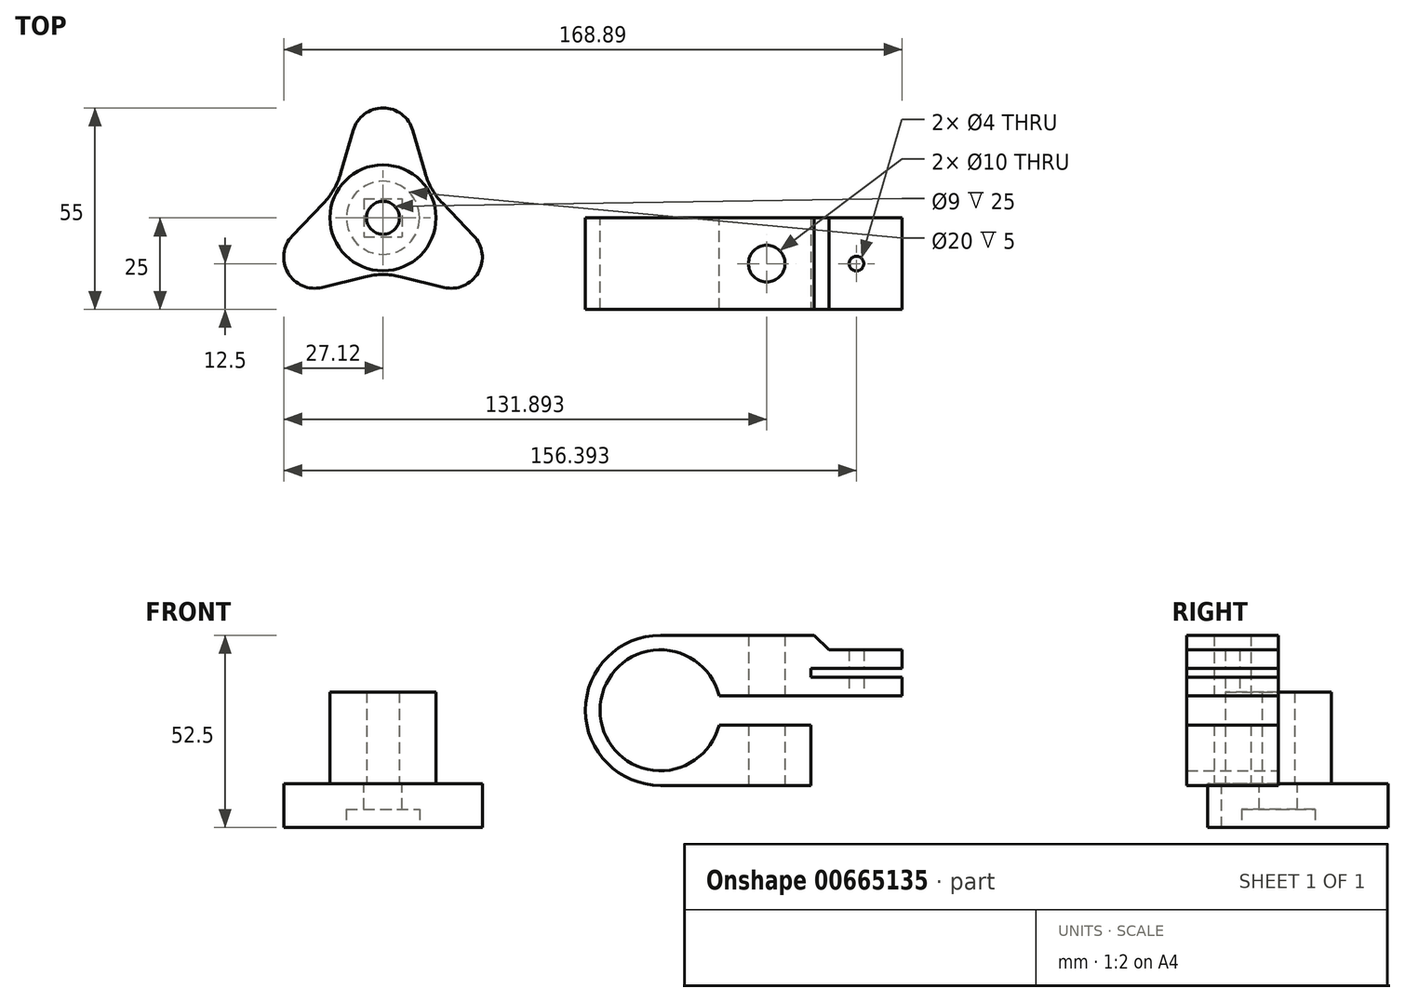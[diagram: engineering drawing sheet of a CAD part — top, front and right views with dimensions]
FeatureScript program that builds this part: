
annotation { "Feature Type Name" : "Feature", "Feature Type Description" : "" }
export const myFeature = defineFeature(function(context is Context, id is Id, definition is map)
    precondition{}
    {
        {
            var Q0;
            Q0=qCreatedBy(makeId("Top.planeOp"),FACE);
            var sketch = newSketch(context, id + "F0", { "sketchPlane" : qUnion([Q0])});
            skLineSegment(sketch, "E0.bottom", {"start": v(-5.25, 5.25) * mm, "end": v(5.25, 5.25) * mm});
            skLineSegment(sketch, "E0.top", {"start": v(-5.25, -5.25) * mm, "end": v(5.25, -5.25) * mm});
            skLineSegment(sketch, "E0.left", {"start": v(-5.25, 5.25) * mm, "end": v(-5.25, -5.25) * mm});
            skLineSegment(sketch, "E0.right", {"start": v(5.25, 5.25) * mm, "end": v(5.25, -5.25) * mm});
            skLineSegment(sketch, "E1", {"start": v(5.25, -5.25) * mm, "end": v(-5.25, 5.25) * mm, "construction": true});
            skCircle(sketch, "E2", {"center": v(0, 0) * mm, "radius": 14.47 * mm});
            skArc(sketch, "E3", {"start": v(8.15, 23.88) * mm, "mid": v(0, 30) * mm, "end": v(-8.15, 23.88) * mm});
            skLineSegment(sketch, "E4", {"start": v(-8.15, 23.88) * mm, "end": v(-11.53, 12.19) * mm});
            skLineSegment(sketch, "E5", {"start": v(8.15, 23.88) * mm, "end": v(11.53, 12.19) * mm});
            skArc(sketch, "E6.1.0", {"start": v(-24.75, -4.88) * mm, "mid": v(-25.98, -15) * mm, "end": v(-16.6, -19) * mm});
            skLineSegment(sketch, "E6.1.1", {"start": v(-24.75, -4.88) * mm, "end": v(-16.32, 3.9) * mm});
            skLineSegment(sketch, "E6.1.2", {"start": v(-16.6, -19) * mm, "end": v(-4.79, -16.08) * mm});
            skArc(sketch, "E6.2.0", {"start": v(16.6, -19) * mm, "mid": v(25.98, -15) * mm, "end": v(24.75, -4.88) * mm});
            skLineSegment(sketch, "E6.2.1", {"start": v(16.6, -19) * mm, "end": v(4.79, -16.08) * mm});
            skLineSegment(sketch, "E6.2.2", {"start": v(24.75, -4.88) * mm, "end": v(16.32, 3.9) * mm});
            skPoint(sketch, "E7.orphan", {"position": v(-10.43, 10.02) * mm});
            skPoint(sketch, "E8.orphan", {"position": v(-17.5, -8.42) * mm});
            skPoint(sketch, "E9.orphan", {"position": v(13.9, 4.02) * mm});
            skPoint(sketch, "E10.orphan", {"position": v(1.46, 19.36) * mm});
            skPoint(sketch, "E11.orphan", {"position": v(16.04, -10.94) * mm});
            skPoint(sketch, "E12.orphan", {"position": v(-3.46, -14.04) * mm});
            skPoint(sketch, "E13.visualSharp", {"position": v(-12.9, 7.45) * mm});
            skArc(sketch, "E13.filletArc", {"start": v(-16.32, 3.9) * mm, "mid": v(-13.42, 7.75) * mm, "end": v(-11.53, 12.19) * mm});
            skPoint(sketch, "E14.visualSharp", {"position": v(12.9, 7.45) * mm});
            skArc(sketch, "E14.filletArc", {"start": v(11.53, 12.19) * mm, "mid": v(13.42, 7.75) * mm, "end": v(16.32, 3.9) * mm});
            skPoint(sketch, "E15.visualSharp", {"position": v(0, -14.9) * mm});
            skArc(sketch, "E15.filletArc", {"start": v(4.79, -16.08) * mm, "mid": v(0, -15.5) * mm, "end": v(-4.79, -16.08) * mm});
            skCircle(sketch, "E16", {"center": v(0, 0) * mm, "radius": 4.5 * mm});
            skSolve(sketch);
        }
        {
            var Q0;
            Q0=makeQuery(id+"F0.imprint","IMPRINT",FACE,{"disambiguationData":[TD([[makeQuery(id+"F0.imprint","IMPRINT",EDGE,{"derivedFrom":sQuery(id+"F0.wireOp",EDGE,"E2")}),-1.0]])]});
            var Q1;
            Q1=makeQuery(id+"F0.imprint","IMPRINT",FACE,{"disambiguationData":[TD([[makeQuery(id+"F0.imprint","IMPRINT",EDGE,{"derivedFrom":sQuery(id+"F0.wireOp",EDGE,"E0.bottom")}),1.0]])]});
            extrude(context, id + "F1", {"entities" : qUnion([Q0, Q1]), "oppositeDirection" : true, "depth" : 12 * mm, "offsetDistance" : 25 * mm});
        }
        {
            var Q0;
            Q0=makeQuery(id+"F0.imprint","IMPRINT",FACE,{"disambiguationData":[TD([[makeQuery(id+"F0.imprint","IMPRINT",EDGE,{"derivedFrom":sQuery(id+"F0.wireOp",EDGE,"E0.bottom")}),1.0]])]});
            var Q1;
            Q1=makeQuery(id+"F0.imprint","IMPRINT",FACE,{"disambiguationData":[TD([[makeQuery(id+"F0.imprint","IMPRINT",EDGE,{"derivedFrom":sQuery(id+"F0.wireOp",EDGE,"E0.bottom")}),-1.0]])]});
            extrude(context, id + "F2", {"entities" : qUnion([Q0, Q1]), "operationType" : NewBodyOperationType.ADD, "depth" : 25 * mm, "offsetDistance" : 25 * mm});
        }
        {
            var Q0;
            Q0=makeQuery(id+"F1.opExtrude","CAP_FACE",FACE,{"disambiguationData":[OSD([sQuery(id+"F0.wireOp",EDGE,"E0.bottom"),sQuery(id+"F0.wireOp",EDGE,"E0.top"),sQuery(id+"F0.wireOp",EDGE,"E0.left"),sQuery(id+"F0.wireOp",EDGE,"E0.right"),sQuery(id+"F0.wireOp",EDGE,"E3"),sQuery(id+"F0.wireOp",EDGE,"E4"),sQuery(id+"F0.wireOp",EDGE,"E5"),sQuery(id+"F0.wireOp",EDGE,"E6.1.0"),sQuery(id+"F0.wireOp",EDGE,"E6.1.1"),sQuery(id+"F0.wireOp",EDGE,"E6.1.2"),sQuery(id+"F0.wireOp",EDGE,"E6.2.0"),sQuery(id+"F0.wireOp",EDGE,"E6.2.1"),sQuery(id+"F0.wireOp",EDGE,"E6.2.2"),sQuery(id+"F0.wireOp",EDGE,"E13.filletArc"),sQuery(id+"F0.wireOp",EDGE,"E14.filletArc"),sQuery(id+"F0.wireOp",EDGE,"E15.filletArc")])],"isStart":false});
            var sketch = newSketch(context, id + "F3", { "sketchPlane" : qUnion([Q0])});
            skCircle(sketch, "E17", {"center": v(0, 0) * mm, "radius": 10 * mm});
            skSolve(sketch);
        }
        {
            var Q0;
            Q0=makeQuery(id+"F3.imprint","IMPRINT",FACE,{"disambiguationData":[TD([[makeQuery(id+"F3.imprint","IMPRINT",EDGE,{"derivedFrom":sQuery(id+"F3.wireOp",EDGE,"E17")}),1.0]])]});
            extrude(context, id + "F4", {"entities" : qUnion([Q0]), "operationType" : NewBodyOperationType.REMOVE, "oppositeDirection" : true, "depth" : 5 * mm, "offsetDistance" : 25 * mm});
        }
        {
            var Q0;
            Q0=qCreatedBy(makeId("Front.planeOp"),FACE);
            var sketch = newSketch(context, id + "F5", { "sketchPlane" : qUnion([Q0])});
            skArc(sketch, "E18", {"start": v(91.77, 24) * mm, "mid": v(59.26, 20) * mm, "end": v(91.77, 16) * mm});
            skLineSegment(sketch, "E19", {"start": v(91.77, 24) * mm, "end": v(116.77, 24) * mm});
            skLineSegment(sketch, "E20", {"start": v(116.77, 24) * mm, "end": v(116.77, 40.5) * mm});
            skLineSegment(sketch, "E21", {"start": v(116.77, 40.5) * mm, "end": v(75.76, 40.5) * mm});
            skArc(sketch, "E22", {"start": v(75.76, 40.5) * mm, "mid": v(55.26, 20) * mm, "end": v(75.76, -0.5) * mm});
            skLineSegment(sketch, "E23", {"start": v(75.76, -0.5) * mm, "end": v(116.77, -0.5) * mm});
            skLineSegment(sketch, "E24", {"start": v(116.77, -0.5) * mm, "end": v(116.77, 16) * mm});
            skLineSegment(sketch, "E25", {"start": v(116.77, 16) * mm, "end": v(91.77, 16) * mm});
            skSolve(sketch);
        }
        {
            var Q0;
            Q0=makeQuery(id+"F5.imprint","IMPRINT",FACE,{"disambiguationData":[TD([[makeQuery(id+"F5.imprint","IMPRINT",EDGE,{"derivedFrom":sQuery(id+"F5.wireOp",EDGE,"E18")}),-1.0]])]});
            extrude(context, id + "F6", {"entities" : qUnion([Q0]), "depth" : 25 * mm, "offsetDistance" : 25 * mm});
        }
        {
            var Q0;
            Q0=makeQuery(id+"F6.opExtrude","SWEPT_FACE",FACE,{"disambiguationData":[OSD([sQuery(id+"F5.wireOp",EDGE,"E20")])]});
            var sketch = newSketch(context, id + "F7", { "sketchPlane" : qUnion([Q0])});
            skLineSegment(sketch, "E26.0", {"start": v(0, 24) * mm, "end": v(0, 40.5) * mm});
            skLineSegment(sketch, "E27.0", {"start": v(-25, 24) * mm, "end": v(0, 24) * mm});
            skLineSegment(sketch, "E28.0", {"start": v(-25, 24) * mm, "end": v(-25, 40.5) * mm});
            skLineSegment(sketch, "E29.0", {"start": v(-25, 40.5) * mm, "end": v(0, 40.5) * mm});
            skLineSegment(sketch, "E30", {"start": v(0, 29) * mm, "end": v(-25, 29) * mm});
            skLineSegment(sketch, "E31", {"start": v(0, 31.5) * mm, "end": v(-25, 31.5) * mm});
            skLineSegment(sketch, "E32", {"start": v(0, 36.5) * mm, "end": v(-25, 36.5) * mm});
            skLineSegment(sketch, "E33", {"start": v(-25, 36.5) * mm, "end": v(-25, 31.5) * mm});
            skLineSegment(sketch, "E34", {"start": v(-25, 29) * mm, "end": v(-25, 24) * mm});
            skLineSegment(sketch, "E35", {"start": v(-25, 36.5) * mm, "end": v(0, 31.5) * mm, "construction": true});
            skLineSegment(sketch, "E36", {"start": v(0, 29) * mm, "end": v(-25, 24) * mm, "construction": true});
            skSolve(sketch);
        }
        {
            var Q0;
            {var subQ0=sQuery(id+"F7.wireOp",EDGE,"E27.0");Q0=makeQuery(id+"F7.imprint","IMPRINT",FACE,{"disambiguationData":[TD([[makeQuery(id+"F7.imprint","IMPRINT",EDGE,{"derivedFrom":subQ0}),1.0]])]});}
            var Q1;
            {var subQ0=sQuery(id+"F7.wireOp",EDGE,"E31");Q1=makeQuery(id+"F7.imprint","IMPRINT",FACE,{"disambiguationData":[TD([[makeQuery(id+"F7.imprint","IMPRINT",EDGE,{"derivedFrom":subQ0}),-1.0]])]});}
            extrude(context, id + "F8", {"entities" : qUnion([Q0, Q1]), "operationType" : NewBodyOperationType.ADD, "depth" : 25 * mm, "offsetDistance" : 25 * mm});
        }
        {
            var Q0;
            Q0=makeQuery(id+"F8.opExtrude","CAP_EDGE",EDGE,{"disambiguationData":[OSD([sQuery(id+"F7.wireOp",EDGE,"E32")])],"isStart":true});
            chamfer(context, id + "F9", {"entities" : qUnion([Q0]), "width" : 5 * mm, "tangentPropagation" : true});
        }
        {
            var Q0;
            Q0=makeQuery(id+"F6.opExtrude","SWEPT_FACE",FACE,{"disambiguationData":[OSD([sQuery(id+"F5.wireOp",EDGE,"E23")])]});
            var sketch = newSketch(context, id + "F10", { "sketchPlane" : qUnion([Q0])});
            skPoint(sketch, "E37.0", {"position": v(116.77, 12.5) * mm});
            skLineSegment(sketch, "E38.0", {"start": v(116.77, 25) * mm, "end": v(116.77, 0) * mm});
            skLineSegment(sketch, "E39", {"start": v(116.77, 12.5) * mm, "end": v(104.77, 12.5) * mm, "construction": true});
            skCircle(sketch, "E40", {"center": v(104.77, 12.5) * mm, "radius": 5 * mm});
            skLineSegment(sketch, "E41", {"start": v(116.77, 12.5) * mm, "end": v(141.77, 12.5) * mm, "construction": true});
            skLineSegment(sketch, "E42.0", {"start": v(141.77, 25) * mm, "end": v(141.77, 0) * mm});
            skCircle(sketch, "E43", {"center": v(129.27, 12.5) * mm, "radius": 2 * mm});
            skSolve(sketch);
        }
        {
            var Q0;
            Q0=makeQuery(id+"F10.imprint","IMPRINT",FACE,{"disambiguationData":[TD([[makeQuery(id+"F10.imprint","IMPRINT",EDGE,{"derivedFrom":sQuery(id+"F10.wireOp",EDGE,"E40")}),1.0]])]});
            var Q1;
            Q1=makeQuery(id+"F10.imprint","IMPRINT",FACE,{"disambiguationData":[TD([[makeQuery(id+"F10.imprint","IMPRINT",EDGE,{"derivedFrom":sQuery(id+"F10.wireOp",EDGE,"E43")}),1.0]])]});
            extrude(context, id + "F11", {"entities" : qUnion([Q0, Q1]), "operationType" : NewBodyOperationType.REMOVE, "endBound" : BoundingType.THROUGH_ALL, "oppositeDirection" : true, "depth" : 25 * mm, "offsetDistance" : 25 * mm});
        }
    });
